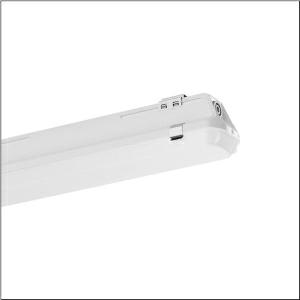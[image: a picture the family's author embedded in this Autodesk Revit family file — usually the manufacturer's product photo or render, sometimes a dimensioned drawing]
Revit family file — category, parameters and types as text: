
# Revit family: monsun_r__21_parking_51fg207p440b_4b42
name_source: partatom
category: Lighting Fixtures
units: mm (PartAtom-declared; Revit-internal decimal feet)

## family parameters
Cut with Voids When Loaded = No
Host = Face
Light Source = No
Part Type = Normal
Room Calculation Point = No
Round Connector Dimension = Use Diameter
Shared = No

## types (1)
- Monsun® 21 parking (1 x LED, 5050 lm, 35.4 W, 4000K)
    Apparent Load = 35 VA
    CIE Flux Codes = 45 75 93 94 100
    Color Rendering = 80
    Color Temperature = 4000K
    Default Elevation = 1800 mm
    Description = Monsun® 21 parking, damp-proof luminaire, chain hanger, primary optical cover: enclosure, of PC, light emission: direct distribution, primary light characteristic: symmetric, installation type: suspended mounting, surface-mounted, horizontal mounting, vertical mounting, LED, rated luminous flux: 5.050lm, luminous efficacy: 143lm/W, light colour: 840, colour temperature: 4000K, control gear: ECG, with terminal, 3-pole, max. 2.5mm², mains connection: 220..240V, AC, 50/60Hz, rated input power: 35W, housing, of glass-fibre reinforced polyester, uncoated, bright grey, incl. chain hanger, length: 1.590mm, width: 90mm, height: 88mm, clip for enclosure, of stainless steel (V2A), ceiling mounting element, of stainless steel (V2A), chain hanger, of stainless steel (V2A), protection rating (complete): IP66, insulation class (complete): insulation class I (protective earthing), certification: CE, ENEC, VDE, UKCA, protection symbol: D, impact resistance: IK08, permissible operating ambient temperature: -25..+35°C, standard: EN 50419, EN 60598-2-1, corresponds to IFS (International Featured Standards) requirements for safety and quality in the food industry, for indoor or canopied outdoor use, no direct snow, no direct sun, no direct rain, contact your sales advisor before using the luminaires in applications with unclear chemical exposure, large temperature fluctuations or condensation-forming humidity, LABS conformity tested according to VDMA 24364:2018-05, packaging unit: 1 piece
    Height = 89 mm
    Lamp = 1 x LED
    Lamp Light Flux = 5050 lm
    Lamp Power = 35.4 W
    Lamp count = 1
    Length = 1590 mm
    Luminous efficacy = 143 lm/W
    Manufacturer = Siteco
    ModVariant = No
    Model = 51FG207P440B
    Mounting Place = Ceiling
    Mounting Type = Surface mounted
    Number of Poles = 1
    OnlyDefault = Yes
    Power Factor = 1
    Product Name = Monsun® 21 parking
    Product group = damp-proof luminaire
    ProductGroupID = 300
    Protection Class = Protection class I
    Protection Degree = IP 66
    RLX_Detail_Level = 1
    RLX_Emergency_Light_Flux = 0 lm
    RLX_Emergency_Type = 0
    RLX_Emergency_Type_DB = No
    RlxData = <blob elided: 88485 chars, md5=2973d183>
    Socket = socket
    Standby Power = 0 W
    System Light Flux = 5050 lm
    System Power = 35 W
    Type Comments = Product without accessories
    Type Image = l_1006717.jpg
    URL = http://relux.com
    VarID = ---
    Voltage = 0 V
    Weight = 0.00 kg
    Width = 90 mm

## geometry (parser evidence)
native form markers: Blend x4, Sweep x12
no freeform markers — native parametric forms only
